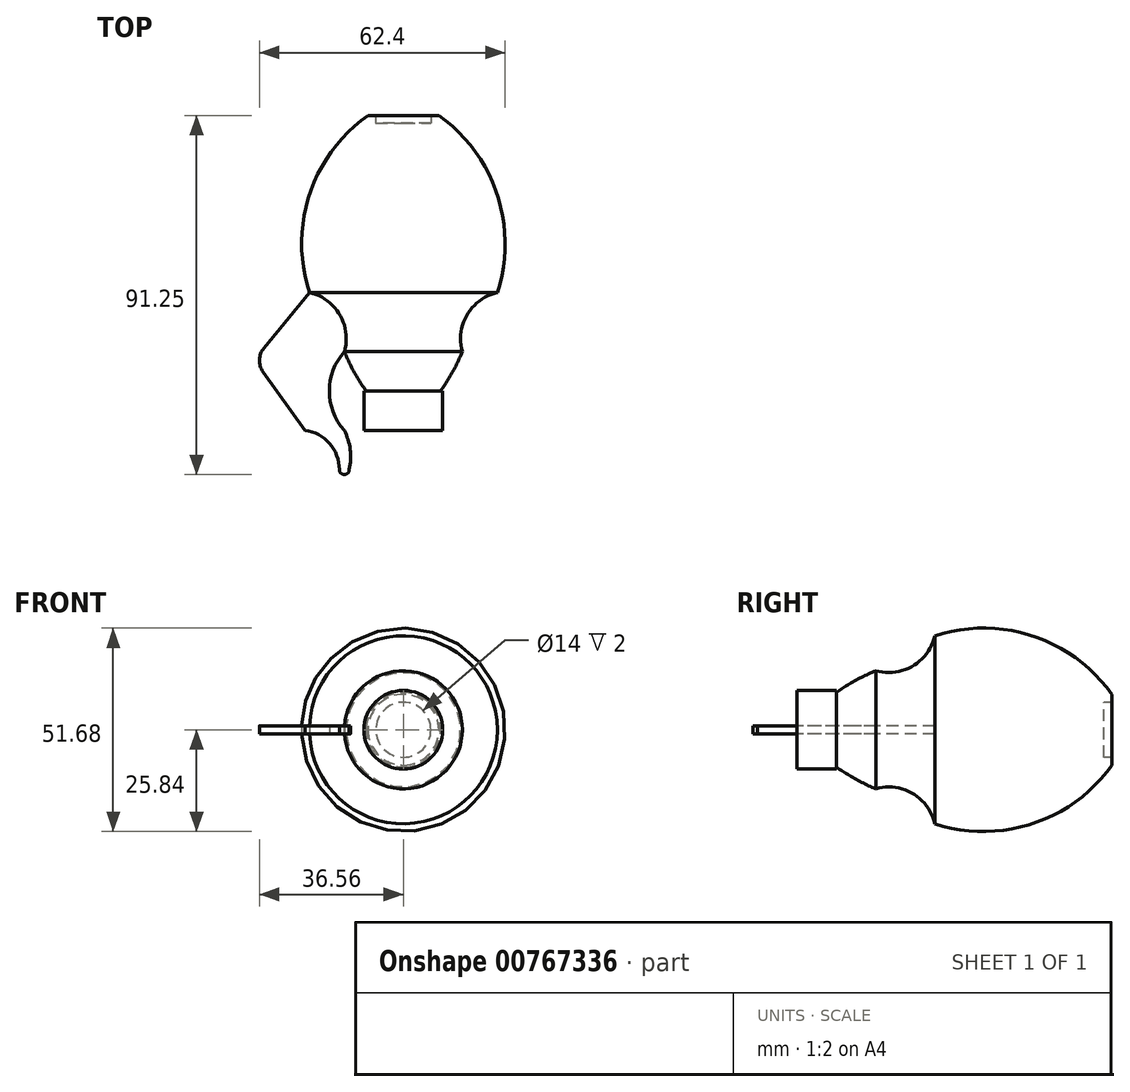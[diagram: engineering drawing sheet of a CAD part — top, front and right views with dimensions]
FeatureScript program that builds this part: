
annotation { "Feature Type Name" : "Feature", "Feature Type Description" : "" }
export const myFeature = defineFeature(function(context is Context, id is Id, definition is map)
    precondition{}
    {
        {
            var Q0;
            Q0=qCreatedBy(makeId("Top.planeOp"),FACE);
            var sketch = newSketch(context, id + "F0", { "sketchPlane" : qUnion([Q0])});
            skLineSegment(sketch, "E0", {"start": v(0, 0) * mm, "end": v(0, 80) * mm});
            skLineSegment(sketch, "E1", {"start": v(0, 80) * mm, "end": v(9, 80) * mm});
            skLineSegment(sketch, "E2", {"start": v(0, 35) * mm, "end": v(23.88, 35) * mm});
            skLineSegment(sketch, "E3", {"start": v(0, 20) * mm, "end": v(15, 20) * mm});
            skArc(sketch, "E4", {"start": v(23.88, 35) * mm, "mid": v(23.82, 59.94) * mm, "end": v(9, 80) * mm});
            skArc(sketch, "E5", {"start": v(23.88, 35) * mm, "mid": v(16.21, 29.41) * mm, "end": v(15, 20) * mm});
            skArc(sketch, "E6", {"start": v(0, 0) * mm, "mid": v(8.77, 9.05) * mm, "end": v(15, 20) * mm});
            skLineSegment(sketch, "E7", {"start": v(0, 78) * mm, "end": v(7, 78) * mm});
            skLineSegment(sketch, "E8", {"start": v(7, 78) * mm, "end": v(7, 80) * mm});
            skPoint(sketch, "E8.endSnap0", {"position": v(4.5, 80) * mm});
            skSolve(sketch);
        }
        {
            var Q0;
            {var subQ2=sQuery(id+"F0.wireOp",EDGE,"E3");Q0=makeQuery(id+"F0.imprint","IMPRINT",FACE,{"disambiguationData":[TD([[makeQuery(id+"F0.imprint","IMPRINT",EDGE,{"derivedFrom":subQ2}),-1.0]])]});}
            var Q1;
            {var subQ0=sQuery(id+"F0.wireOp",EDGE,"E2");Q1=makeQuery(id+"F0.imprint","IMPRINT",FACE,{"disambiguationData":[TD([[makeQuery(id+"F0.imprint","IMPRINT",EDGE,{"derivedFrom":subQ0}),-1.0]])]});}
            var Q2;
            {var subQ1=sQuery(id+"F0.wireOp",EDGE,"E2");Q2=makeQuery(id+"F0.imprint","IMPRINT",FACE,{"disambiguationData":[TD([[makeQuery(id+"F0.imprint","IMPRINT",EDGE,{"derivedFrom":subQ1}),1.0]])]});}
            var Q3;
            Q3=sQuery(id+"F0.wireOp",EDGE,"E0");
            revolve(context, id + "F1", {"surfaceOperationType" : NewSurfaceOperationType.NEW, "entities" : qUnion([Q0, Q1, Q2]), "axis" : qUnion([Q3]), "revolveType" : RevolveType.FULL});
        }
        {
            var Q0;
            Q0=qCreatedBy(makeId("Top.planeOp"),FACE);
            var sketch = newSketch(context, id + "F2", { "sketchPlane" : qUnion([Q0])});
            skLineSegment(sketch, "E9.0", {"start": v(23.88, 35) * mm, "end": v(-23.88, 35) * mm});
            skLineSegment(sketch, "E10.0", {"start": v(15, 20) * mm, "end": v(-15, 20) * mm});
            skLineSegment(sketch, "E11", {"start": v(-23.88, 35) * mm, "end": v(-15, 20) * mm});
            skLineSegment(sketch, "E12", {"start": v(0, 35) * mm, "end": v(0, 20) * mm});
            skSolve(sketch);
        }
        {
            var Q0;
            Q0 = qSketchRegion(id + "F2", true);
            extrude(context, id + "F3", {"entities" : qUnion([Q0]), "operationType" : NewBodyOperationType.ADD, "endBound" : BoundingType.SYMMETRIC, "depth" : 2 * mm, "offsetDistance" : 25 * mm});
        }
        {
            var Q0;
            Q0=qCreatedBy(makeId("Top.planeOp"),FACE);
            var sketch = newSketch(context, id + "F4", { "sketchPlane" : qUnion([Q0])});
            skLineSegment(sketch, "E13", {"start": v(0, 0) * mm, "end": v(0, -10) * mm});
            skLineSegment(sketch, "E14", {"start": v(0, -10) * mm, "end": v(-15, -10) * mm});
            skLineSegment(sketch, "E15", {"start": v(-15, -10) * mm, "end": v(-15, 0) * mm});
            skLineSegment(sketch, "E16", {"start": v(-15, 0) * mm, "end": v(-25, 0) * mm});
            skArc(sketch, "E17", {"start": v(-16.25, -10) * mm, "mid": v(-15, -11.25) * mm, "end": v(-13.75, -10) * mm});
            skLineSegment(sketch, "E18", {"start": v(-15, -10) * mm, "end": v(-16.25, -10) * mm});
            skFitSpline(sketch, "E19.0", {"points": [v(-23.86, 35) * mm, v(-23.46, 34.91) * mm, v(-22.67, 34.69) * mm, v(-21.54, 34.24) * mm, v(-20.46, 33.68) * mm, v(-19.6, 33.13) * mm, v(-18.96, 32.63) * mm, v(-18.34, 32.1) * mm, v(-17.62, 31.39) * mm, v(-16.85, 30.45) * mm, v(-16.16, 29.42) * mm, v(-15.6, 28.35) * mm, v(-15.22, 27.4) * mm, v(-14.97, 26.63) * mm, v(-14.76, 25.84) * mm, v(-14.62, 25.04) * mm, v(-14.53, 24.22) * mm, v(-14.5, 23.4) * mm, v(-14.53, 21.98) * mm, v(-14.74, 20.79) * mm, v(-14.97, 20) * mm]});
            skArc(sketch, "E20", {"start": v(-14.97, 20) * mm, "mid": v(-18.8, 10) * mm, "end": v(-15, 0) * mm});
            skArc(sketch, "E21", {"start": v(-13.75, -10) * mm, "mid": v(-13.51, -4.9) * mm, "end": v(-15, 0) * mm});
            skArc(sketch, "E22", {"start": v(-16.25, -10) * mm, "mid": v(-18.75, -3.36) * mm, "end": v(-25, 0) * mm});
            skLineSegment(sketch, "E23", {"start": v(-23.86, 35) * mm, "end": v(-35.42, 20.91) * mm});
            skLineSegment(sketch, "E24", {"start": v(-35.62, 14.83) * mm, "end": v(-25, 0) * mm});
            skPoint(sketch, "E25.visualSharp", {"position": v(-37.86, 17.94) * mm});
            skArc(sketch, "E25.filletArc", {"start": v(-35.42, 20.91) * mm, "mid": v(-36.55, 17.9) * mm, "end": v(-35.62, 14.83) * mm});
            skSolve(sketch);
        }
        {
            var Q0;
            Q0=makeQuery(id+"F4.imprint","IMPRINT",FACE,{"disambiguationData":[TD([[makeQuery(id+"F4.imprint","IMPRINT",EDGE,{"derivedFrom":sQuery(id+"F4.wireOp",EDGE,"E16")}),-1.0]])]});
            var Q1;
            Q1=makeQuery(id+"F4.imprint","IMPRINT",FACE,{"disambiguationData":[TD([[makeQuery(id+"F4.imprint","IMPRINT",EDGE,{"derivedFrom":sQuery(id+"F4.wireOp",EDGE,"E15")}),1.0]])]});
            var Q2;
            {var subQ0=sQuery(id+"F4.wireOp",EDGE,"E15");Q2=makeQuery(id+"F4.imprint","IMPRINT",FACE,{"disambiguationData":[TD([[makeQuery(id+"F4.imprint","IMPRINT",EDGE,{"derivedFrom":subQ0}),-1.0]])]});}
            var Q3;
            {var subQ2=sQuery(id+"F4.wireOp",EDGE,"E17");Q3=makeQuery(id+"F4.imprint","IMPRINT",FACE,{"disambiguationData":[TD([[makeQuery(id+"F4.imprint","IMPRINT",EDGE,{"derivedFrom":subQ2}),1.0]])]});}
            extrude(context, id + "F5", {"entities" : qUnion([Q0, Q1, Q2, Q3]), "operationType" : NewBodyOperationType.ADD, "endBound" : BoundingType.SYMMETRIC, "depth" : 2 * mm, "offsetDistance" : 25 * mm});
        }
        {
            var Q0;
            Q0=qCreatedBy(makeId("Front.planeOp"),FACE);
            var sketch = newSketch(context, id + "F6", { "sketchPlane" : qUnion([Q0])});
            skCircle(sketch, "E26", {"center": v(0, 0) * mm, "radius": 10 * mm});
            skSolve(sketch);
        }
        {
            var Q0;
            Q0 = qSketchRegion(id + "F6", true);
            extrude(context, id + "F7", {"entities" : qUnion([Q0]), "operationType" : NewBodyOperationType.ADD, "oppositeDirection" : true, "depth" : 10 * mm, "offsetDistance" : 25 * mm});
        }
    });
